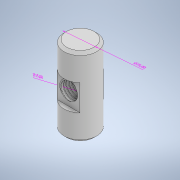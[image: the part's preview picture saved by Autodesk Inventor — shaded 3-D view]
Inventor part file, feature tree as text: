
AUTODESK INVENTOR PART (.ipt)
format: ipt  version: 2021 (Build 250183000, 183)  size: 478,720 bytes
history: native  units: mm
features: sketch x6, extrude x4, other x3, chamfer x1, helix x1
ambient origin geometry x8: Origin, YZ Plane, XZ Plane, XY Plane, X Axis, Y Axis, Z Axis, Center Point
bodies: Solid1 (feature_tree)
feature tree (15):
  other  "Annotations"
  extrude  "Extrusion1"  Depth=60.0mm TaperAngle=0.0deg
  extrude  "Extrusion2"  Depth=15.0mm
  chamfer  "Chamfer1"  Distance=60.0mm
  extrude  "Extrusion3"  Depth=2.0mm
  extrude  "Extrusion4"  Depth=20.0mm
  helix  "Coil1"  [1 undecoded]
  sketch  "Sketch1"  dims[d0=25.0mm d1=60.0mm d2=0.0mm]
  sketch  "Sketch2"  dims[d3=30.0mm d4=15.0mm d5=60.0mm d6=0.0mm]
  sketch  "Sketch3"  dims[d17=2.0mm d18=2.0mm d19=45.0deg d20=20.0mm]
  sketch  "Sketch5"  dims[d21=9.0mm d22=20.0mm d23=18.0mm]
  sketch  "Sketch6"  dims[d24=25.0mm d25=0.0mm]
  sketch  "Sketch7"  dims[d30=15.0mm d31=12.835mm d32=18.0mm d33=0.0mm d34=9.0mm d37=1.0mm d40=1.0mm d41=0.126mm d42=60.0deg d43=60.0deg d44=18.0mm d45=2.0mm d46=10.0mm d47=100.0mm d48=0.0mm d49=90.0deg d50=90.0deg d51=0.0mm d52=0.0mm d11=32.163483mm d12=8.638101mm d13=1.058985mm d14=15.0mm d15=32.262659mm d16=25.0mm]
  other  "Diameter Dimension 2"
  other  "Diameter Dimension 3"
note: 1 required parameter value undecoded (feature->parameter linkage not recoverable at this tier; creation-order binding heuristic only, values carry confidence <= 0.55)
